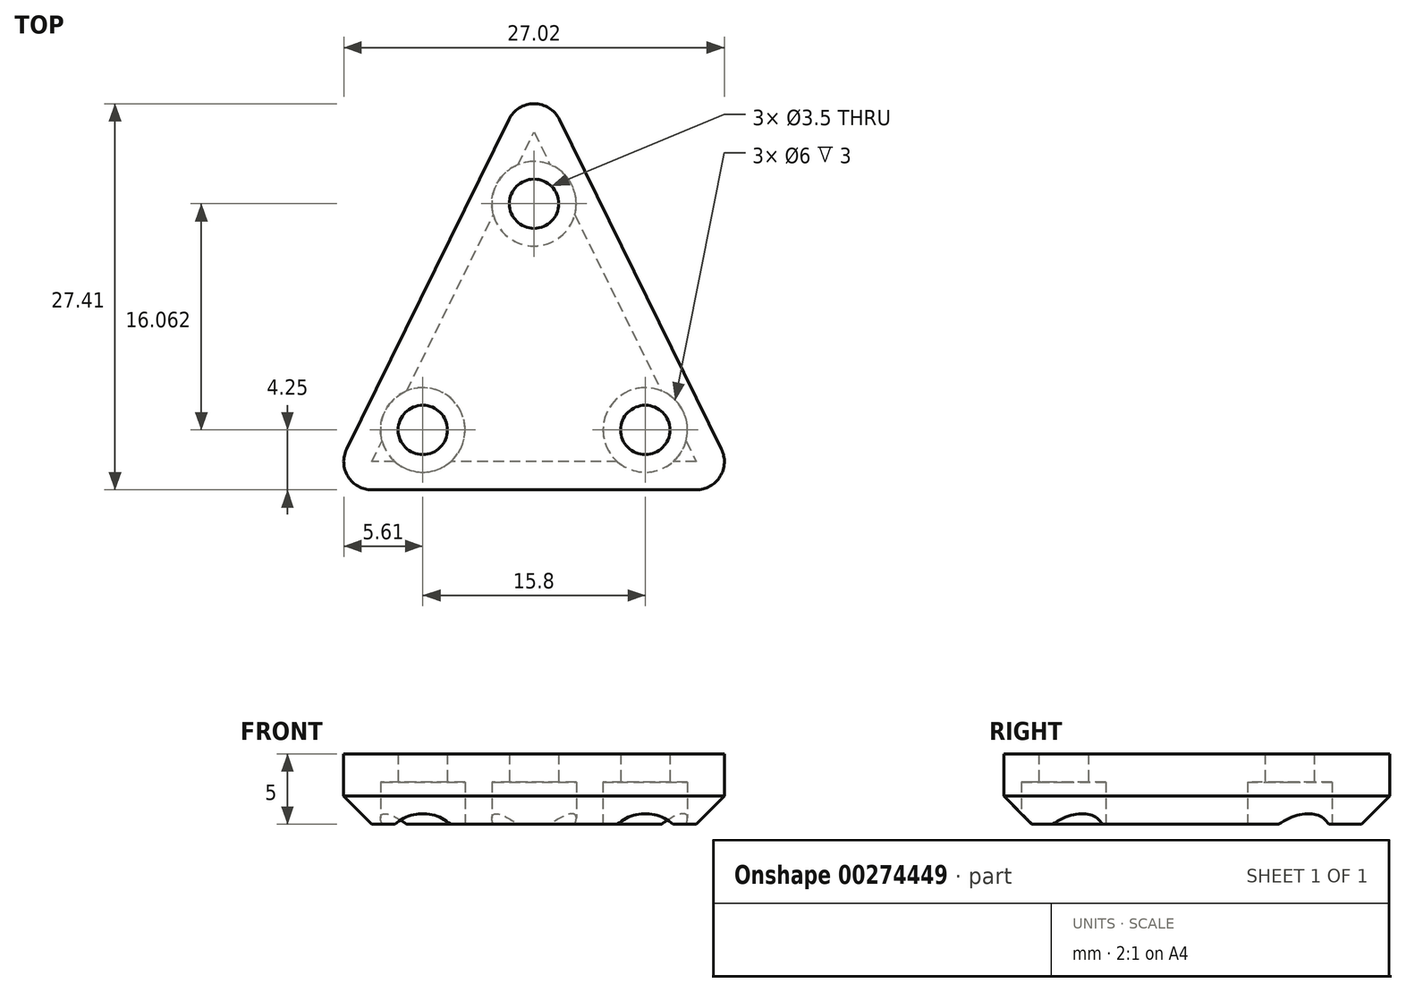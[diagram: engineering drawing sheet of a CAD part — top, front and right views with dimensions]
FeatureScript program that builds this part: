
annotation { "Feature Type Name" : "Feature", "Feature Type Description" : "" }
export const myFeature = defineFeature(function(context is Context, id is Id, definition is map)
    precondition{}
    {
        {
            var Q0;
            Q0=qCreatedBy(makeId("Top.planeOp"),FACE);
            var sketch = newSketch(context, id + "F0", { "sketchPlane" : qUnion([Q0])});
            skPoint(sketch, "E0.start.orphan", {"position": v(7.9, 0) * mm});
            skLineSegment(sketch, "E1.0", {"start": v(-5.4, -1.37) * mm, "end": v(6.1, 22.04) * mm});
            skLineSegment(sketch, "E1.1", {"start": v(-3.61, -4.25) * mm, "end": v(19.41, -4.25) * mm});
            skLineSegment(sketch, "E1.2", {"start": v(21.2, -1.37) * mm, "end": v(9.7, 22.04) * mm});
            skCircle(sketch, "E2", {"center": v(0, 0) * mm, "radius": 1.75 * mm});
            skCircle(sketch, "E3", {"center": v(15.8, 0) * mm, "radius": 1.75 * mm});
            skCircle(sketch, "E4", {"center": v(7.9, 16.06) * mm, "radius": 1.75 * mm});
            skPoint(sketch, "E5.visualSharp", {"position": v(7.9, 25.7) * mm});
            skArc(sketch, "E5.filletArc", {"start": v(9.7, 22.04) * mm, "mid": v(7.9, 23.16) * mm, "end": v(6.1, 22.04) * mm});
            skPoint(sketch, "E6.visualSharp", {"position": v(22.63, -4.25) * mm});
            skArc(sketch, "E6.filletArc", {"start": v(19.41, -4.25) * mm, "mid": v(21.11, -3.3) * mm, "end": v(21.2, -1.37) * mm});
            skPoint(sketch, "E7.visualSharp", {"position": v(-6.83, -4.25) * mm});
            skArc(sketch, "E7.filletArc", {"start": v(-5.4, -1.37) * mm, "mid": v(-5.31, -3.3) * mm, "end": v(-3.61, -4.25) * mm});
            skSolve(sketch);
        }
        {
            var Q0;
            Q0=makeQuery(id+"F0.imprint","IMPRINT",FACE,{"disambiguationData":[TD([[makeQuery(id+"F0.imprint","IMPRINT",EDGE,{"derivedFrom":sQuery(id+"F0.wireOp",EDGE,"E1.0")}),-1.0]])]});
            extrude(context, id + "F1", {"entities" : qUnion([Q0]), "depth" : 5 * mm});
        }
        {
            var Q0;
            Q0=qCreatedBy(makeId("Top.planeOp"),FACE);
            var sketch = newSketch(context, id + "F2", { "sketchPlane" : qUnion([Q0])});
            skCircle(sketch, "E8.0", {"center": v(7.9, 16.06) * mm, "radius": 3 * mm});
            skCircle(sketch, "E9.0", {"center": v(15.8, 0) * mm, "radius": 3 * mm});
            skCircle(sketch, "E10.0", {"center": v(0, 0) * mm, "radius": 3 * mm});
            skSolve(sketch);
        }
        {
            var Q0;
            Q0=makeQuery(id+"F2.imprint","IMPRINT",FACE,{"disambiguationData":[TD([[makeQuery(id+"F2.imprint","IMPRINT",EDGE,{"derivedFrom":sQuery(id+"F2.wireOp",EDGE,"E9.0")}),1.0]])]});
            var Q1;
            Q1=makeQuery(id+"F2.imprint","IMPRINT",FACE,{"disambiguationData":[TD([[makeQuery(id+"F2.imprint","IMPRINT",EDGE,{"derivedFrom":sQuery(id+"F2.wireOp",EDGE,"E10.0")}),1.0]])]});
            var Q2;
            Q2=makeQuery(id+"F2.imprint","IMPRINT",FACE,{"disambiguationData":[TD([[makeQuery(id+"F2.imprint","IMPRINT",EDGE,{"derivedFrom":sQuery(id+"F2.wireOp",EDGE,"E8.0")}),1.0]])]});
            extrude(context, id + "F3", {"entities" : qUnion([Q0, Q1, Q2]), "operationType" : NewBodyOperationType.REMOVE, "depth" : 3 * mm});
        }
        {
            var Q0;
            Q0=makeQuery(id+"F1.opExtrude","CAP_EDGE",EDGE,{"disambiguationData":[OSD([sQuery(id+"F0.wireOp",EDGE,"E1.1")])],"isStart":true});
            chamfer(context, id + "F4", {"entities" : qUnion([Q0]), "width" : 2 * mm, "tangentPropagation" : true});
        }
    });
